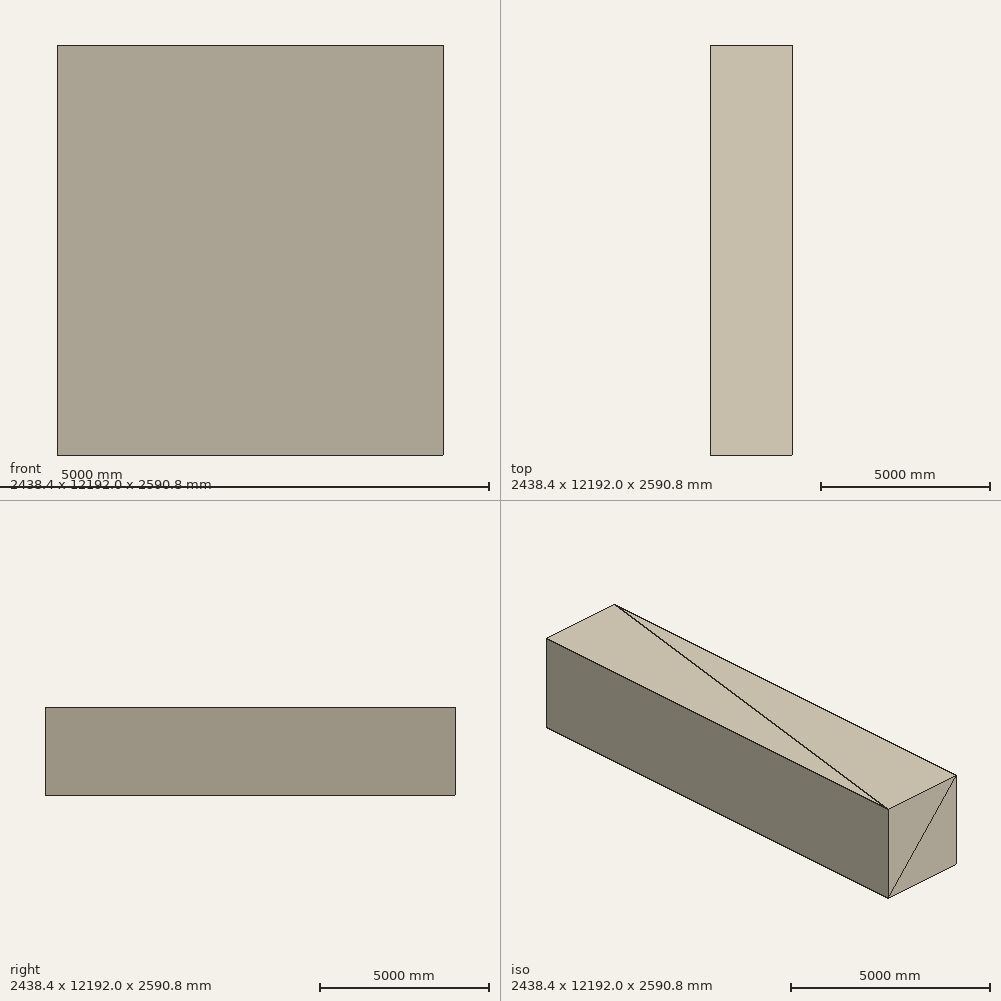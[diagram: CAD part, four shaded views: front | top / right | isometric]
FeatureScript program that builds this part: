
annotation { "Feature Type Name" : "Feature", "Feature Type Description" : "" }
export const myFeature = defineFeature(function(context is Context, id is Id, definition is map)
    precondition{}
    {
        {
            var Q0;
            Q0=qCreatedBy(makeId("Front.planeOp"),FACE);
            var sketch = newSketch(context, id + "F0", { "sketchPlane" : qUnion([Q0])});
            skLineSegment(sketch, "E0.bottom", {"start": v(0, 0) * mm, "end": v(2438.4, 0) * mm});
            skLineSegment(sketch, "E0.top", {"start": v(0, 2590.8) * mm, "end": v(2438.4, 2590.8) * mm});
            skLineSegment(sketch, "E0.left", {"start": v(0, 0) * mm, "end": v(0, 2590.8) * mm});
            skLineSegment(sketch, "E0.right", {"start": v(2438.4, 0) * mm, "end": v(2438.4, 2590.8) * mm});
            skSolve(sketch);
        }
        {
            var Q0;
            Q0=makeQuery(id+"F0.imprint","IMPRINT",FACE,{"disambiguationData":[TD([[makeQuery(id+"F0.imprint","IMPRINT",EDGE,{"derivedFrom":sQuery(id+"F0.wireOp",EDGE,"E0.bottom")}),1.0]])]});
            extrude(context, id + "F1", {"entities" : qUnion([Q0]), "depth" : 12192 * mm, "offsetDistance" : 25.4 * mm});
        }
    });
